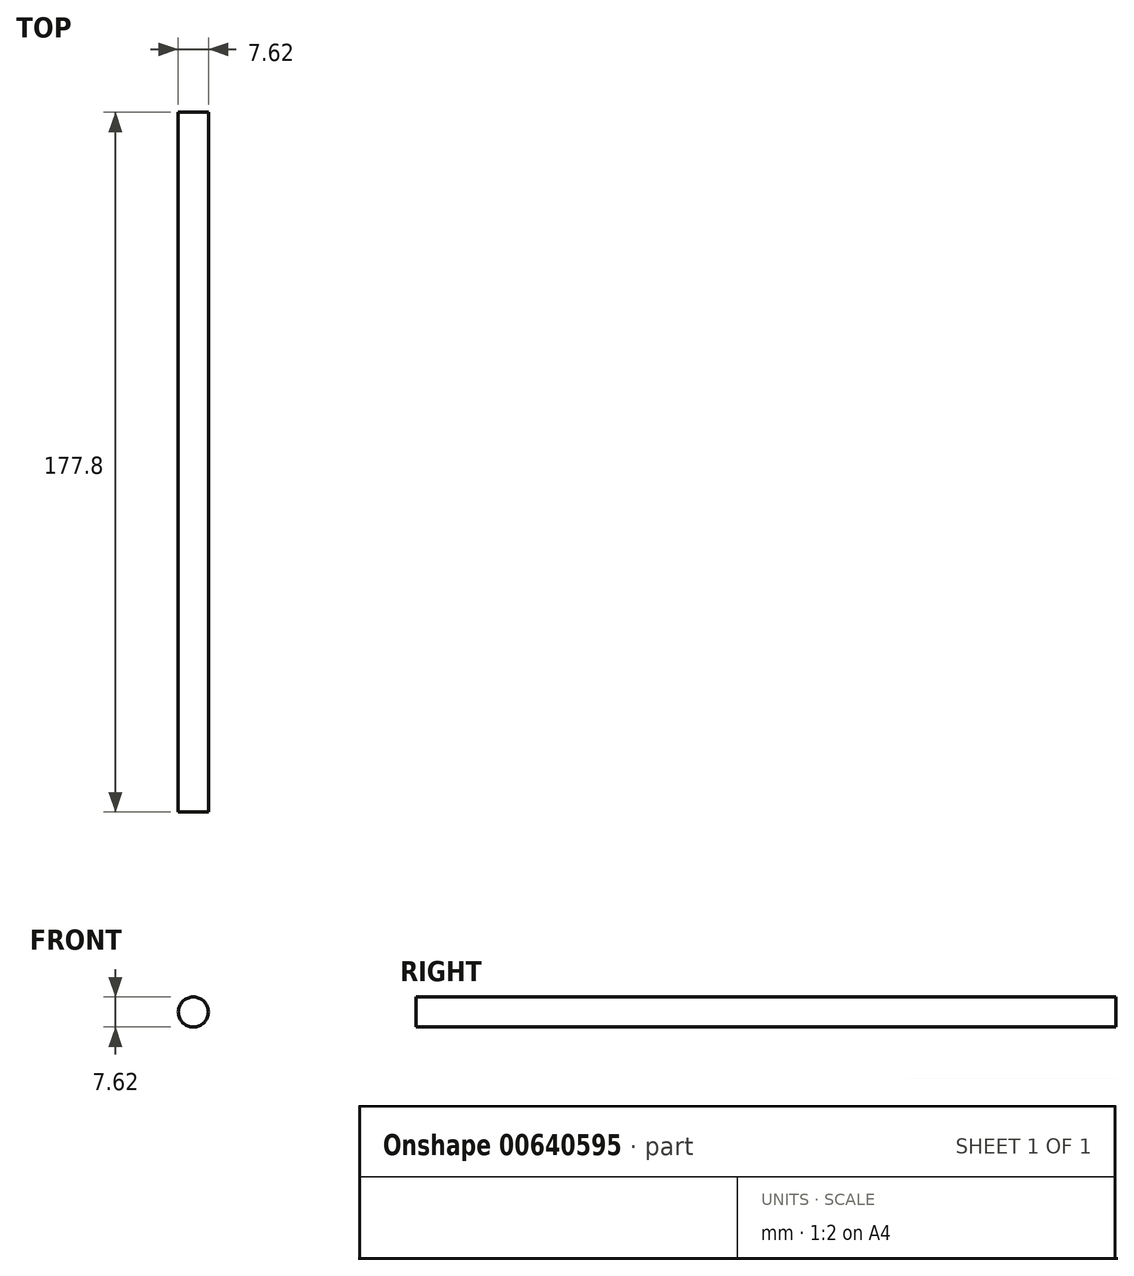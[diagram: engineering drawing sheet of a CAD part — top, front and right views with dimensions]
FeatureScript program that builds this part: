
annotation { "Feature Type Name" : "Feature", "Feature Type Description" : "" }
export const myFeature = defineFeature(function(context is Context, id is Id, definition is map)
    precondition{}
    {
        {
            var Q0;
            Q0=qCreatedBy(makeId("Front.planeOp"),FACE);
            var sketch = newSketch(context, id + "F0", { "sketchPlane" : qUnion([Q0])});
            skCircle(sketch, "E0", {"center": v(0, 0) * mm, "radius": 3.81 * mm});
            skSolve(sketch);
        }
        {
            var Q0;
            Q0=makeQuery(id+"F0.imprint","IMPRINT",FACE,{"disambiguationData":[TD([[makeQuery(id+"F0.imprint","IMPRINT",EDGE,{"derivedFrom":sQuery(id+"F0.wireOp",EDGE,"E0")}),1.0]])]});
            extrude(context, id + "F1", {"entities" : qUnion([Q0]), "depth" : 177.8 * mm, "offsetDistance" : 25.4 * mm});
        }
    });
